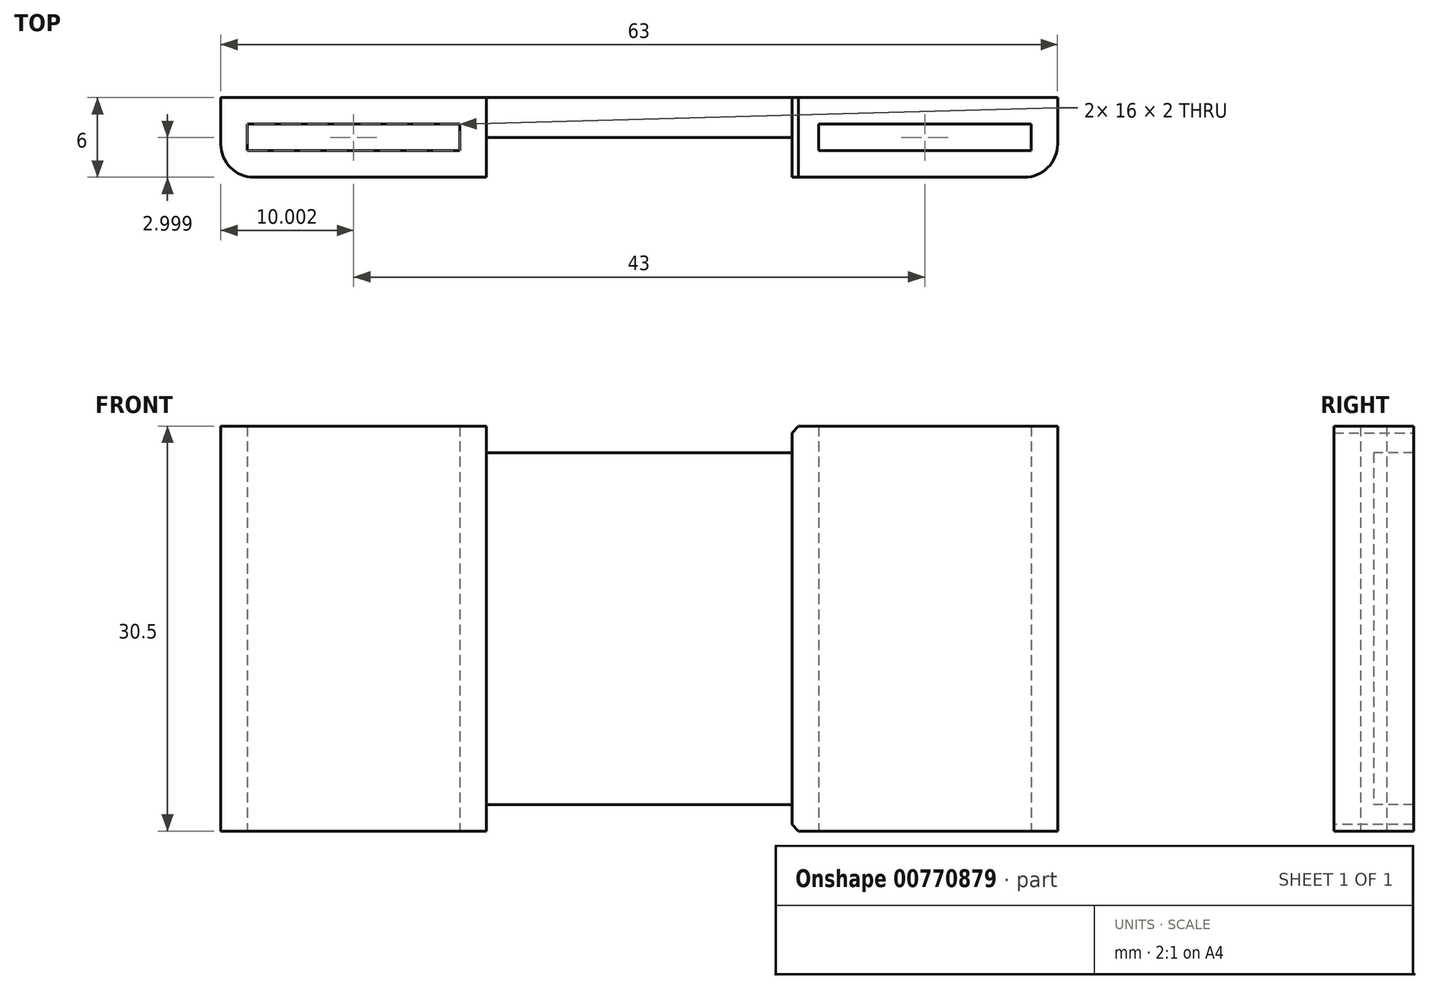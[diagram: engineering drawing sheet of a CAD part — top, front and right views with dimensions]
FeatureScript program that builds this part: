
annotation { "Feature Type Name" : "Feature", "Feature Type Description" : "" }
export const myFeature = defineFeature(function(context is Context, id is Id, definition is map)
    precondition{}
    {
        {
            var Q0;
            Q0=qCreatedBy(makeId("Top.planeOp"),FACE);
            var sketch = newSketch(context, id + "F0", { "sketchPlane" : qUnion([Q0])});
            skLineSegment(sketch, "E0.bottom", {"start": v(-8.67, 15.89) * mm, "end": v(54.33, 15.89) * mm});
            skLineSegment(sketch, "E0.top", {"start": v(11.33, 12.89) * mm, "end": v(34.33, 12.89) * mm});
            skLineSegment(sketch, "E1.top", {"start": v(-8.67, 9.89) * mm, "end": v(11.33, 9.89) * mm});
            skLineSegment(sketch, "E1.right", {"start": v(11.33, 12.89) * mm, "end": v(11.33, 9.89) * mm});
            skLineSegment(sketch, "E2.top", {"start": v(34.33, 9.89) * mm, "end": v(54.33, 9.89) * mm});
            skLineSegment(sketch, "E2.left", {"start": v(34.33, 12.89) * mm, "end": v(34.33, 9.89) * mm});
            skLineSegment(sketch, "E3", {"start": v(-8.67, 15.89) * mm, "end": v(-8.67, 9.89) * mm});
            skLineSegment(sketch, "E4", {"start": v(54.33, 15.89) * mm, "end": v(54.33, 9.89) * mm});
            skLineSegment(sketch, "E5.bottom", {"start": v(-6.67, 13.89) * mm, "end": v(9.33, 13.89) * mm});
            skLineSegment(sketch, "E5.top", {"start": v(-6.67, 11.89) * mm, "end": v(9.33, 11.89) * mm});
            skLineSegment(sketch, "E5.left", {"start": v(-6.67, 13.89) * mm, "end": v(-6.67, 11.89) * mm});
            skLineSegment(sketch, "E5.right", {"start": v(9.33, 13.89) * mm, "end": v(9.33, 11.89) * mm});
            skLineSegment(sketch, "E6.1.0.0", {"start": v(52.33, 13.89) * mm, "end": v(52.33, 11.89) * mm});
            skLineSegment(sketch, "E6.1.0.1", {"start": v(36.33, 13.89) * mm, "end": v(52.33, 13.89) * mm});
            skLineSegment(sketch, "E6.1.0.2", {"start": v(36.33, 11.89) * mm, "end": v(52.33, 11.89) * mm});
            skLineSegment(sketch, "E6.1.0.3", {"start": v(36.33, 13.89) * mm, "end": v(36.33, 11.89) * mm});
            skLineSegment(sketch, "E6.2.0.0", {"start": v(95.33, 13.89) * mm, "end": v(95.33, 11.89) * mm});
            skLineSegment(sketch, "E6.2.0.1", {"start": v(79.33, 13.89) * mm, "end": v(95.33, 13.89) * mm});
            skLineSegment(sketch, "E6.2.0.2", {"start": v(79.33, 11.89) * mm, "end": v(95.33, 11.89) * mm});
            skLineSegment(sketch, "E6.2.0.3", {"start": v(79.33, 13.89) * mm, "end": v(79.33, 11.89) * mm});
            skLineSegment(sketch, "E6.direction1", {"start": v(-6.67, 11.89) * mm, "end": v(36.33, 11.89) * mm, "construction": true});
            skSolve(sketch);
        }
        {
            var Q0;
            Q0=makeQuery(id+"F0.imprint","IMPRINT",FACE,{"disambiguationData":[TD([[makeQuery(id+"F0.imprint","IMPRINT",EDGE,{"derivedFrom":sQuery(id+"F0.wireOp",EDGE,"E0.bottom")}),-1.0]])]});
            extrude(context, id + "F1", {"entities" : qUnion([Q0]), "depth" : 30.5 * mm, "offsetDistance" : 25 * mm});
        }
        {
            var Q0;
            Q0=makeQuery(id+"F1.opExtrude","SWEPT_EDGE",EDGE,{"disambiguationData":[OSD([sQuery(id+"F0.wireOp",EDGE,"E1.top"),sQuery(id+"F0.wireOp",EDGE,"E3")])]});
            var Q1;
            Q1=makeQuery(id+"F1.opExtrude","SWEPT_EDGE",EDGE,{"disambiguationData":[OSD([sQuery(id+"F0.wireOp",EDGE,"E2.top"),sQuery(id+"F0.wireOp",EDGE,"E4")])]});
            fillet(context, id + "F2", {"entities" : qUnion([Q0, Q1]), "radius" : 2.5 * mm, "tangentPropagation" : true, "allowEdgeOverflow" : false});
        }
        {
            var Q0;
            Q0=makeQuery(id+"F1.opExtrude","SWEPT_FACE",FACE,{"disambiguationData":[OSD([sQuery(id+"F0.wireOp",EDGE,"E0.top")])]});
            var sketch = newSketch(context, id + "F3", { "sketchPlane" : qUnion([Q0])});
            skLineSegment(sketch, "E7.bottom", {"start": v(11.33, 30.5) * mm, "end": v(34.33, 30.5) * mm});
            skLineSegment(sketch, "E7.top", {"start": v(11.33, 28.5) * mm, "end": v(34.33, 28.5) * mm});
            skLineSegment(sketch, "E7.left", {"start": v(11.33, 30.5) * mm, "end": v(11.33, 28.5) * mm});
            skLineSegment(sketch, "E7.right", {"start": v(34.33, 30.5) * mm, "end": v(34.33, 28.5) * mm});
            skLineSegment(sketch, "E8.1.0.0", {"start": v(11.33, 2) * mm, "end": v(11.33, 0) * mm});
            skLineSegment(sketch, "E8.1.0.1", {"start": v(11.33, 2) * mm, "end": v(34.33, 2) * mm});
            skLineSegment(sketch, "E8.1.0.2", {"start": v(11.33, 0) * mm, "end": v(34.33, 0) * mm});
            skLineSegment(sketch, "E8.1.0.3", {"start": v(34.33, 2) * mm, "end": v(34.33, 0) * mm});
            skLineSegment(sketch, "E8.2.0.0", {"start": v(11.33, -26.5) * mm, "end": v(11.33, -28.5) * mm});
            skLineSegment(sketch, "E8.2.0.1", {"start": v(11.33, -26.5) * mm, "end": v(34.33, -26.5) * mm});
            skLineSegment(sketch, "E8.2.0.2", {"start": v(11.33, -28.5) * mm, "end": v(34.33, -28.5) * mm});
            skLineSegment(sketch, "E8.2.0.3", {"start": v(34.33, -26.5) * mm, "end": v(34.33, -28.5) * mm});
            skLineSegment(sketch, "E8.direction1", {"start": v(11.33, 28.5) * mm, "end": v(11.33, 0) * mm, "construction": true});
            skSolve(sketch);
        }
        {
            var Q0;
            {var subQ0=sQuery(id+"F3.wireOp",EDGE,"E8.1.0.3");Q0=makeQuery(id+"F3.imprint","IMPRINT",FACE,{"disambiguationData":[TD([[makeQuery(id+"F3.imprint","IMPRINT",EDGE,{"derivedFrom":subQ0}),-1.0]])]});}
            var Q1;
            Q1=makeQuery(id+"F3.imprint","IMPRINT",FACE,{"disambiguationData":[TD([[makeQuery(id+"F3.imprint","IMPRINT",EDGE,{"derivedFrom":sQuery(id+"F3.wireOp",EDGE,"E7.bottom")}),-1.0]])]});
            extrude(context, id + "F4", {"entities" : qUnion([Q0, Q1]), "operationType" : NewBodyOperationType.REMOVE, "oppositeDirection" : true, "depth" : 25 * mm, "offsetDistance" : 25 * mm});
        }
        {
            var Q0;
            Q0=makeQuery(id+"F4.boolean.opBoolean","MERGE",EDGE,{"derivedFrom":[makeQuery(id+"F1.opExtrude","CAP_EDGE",EDGE,{"disambiguationData":[OSD([sQuery(id+"F0.wireOp",EDGE,"E1.right")])],"isStart":false}),makeQuery(id+"F4.opExtrude","SWEPT_EDGE",EDGE,{"disambiguationData":[OSD([sQuery(id+"F3.wireOp",EDGE,"E7.bottom"),sQuery(id+"F3.wireOp",EDGE,"E7.left")])]})]});
            var Q1;
            Q1=makeQuery(id+"F4.boolean.opBoolean","MERGE",EDGE,{"derivedFrom":[makeQuery(id+"F1.opExtrude","CAP_EDGE",EDGE,{"disambiguationData":[OSD([sQuery(id+"F0.wireOp",EDGE,"E2.left")])],"isStart":false}),makeQuery(id+"F4.opExtrude","SWEPT_EDGE",EDGE,{"disambiguationData":[OSD([sQuery(id+"F3.wireOp",EDGE,"E7.bottom"),sQuery(id+"F3.wireOp",EDGE,"E7.right")])]})]});
            var Q2;
            Q2=makeQuery(id+"F4.boolean.opBoolean","COPY",EDGE,{"derivedFrom":makeQuery(id+"F4.opExtrude","SWEPT_EDGE",EDGE,{"disambiguationData":[OSD([sQuery(id+"F0.wireOp",EDGE,"E0.top"),sQuery(id+"F3.wireOp",EDGE,"E8.1.0.2"),sQuery(id+"F3.wireOp",EDGE,"E8.1.0.3")])]})});
            var Q3;
            {var subQ0=sQuery(id+"F0.wireOp",EDGE,"E1.right");Q3=makeQuery(id+"F4.boolean.opBoolean","MERGE",EDGE,{"derivedFrom":[makeQuery(id+"F1.opExtrude","CAP_EDGE",EDGE,{"disambiguationData":[OSD([subQ0])],"isStart":true}),makeQuery(id+"F4.opExtrude","SWEPT_EDGE",EDGE,{"disambiguationData":[OSD([sQuery(id+"F0.wireOp",EDGE,"E0.top"),subQ0,sQuery(id+"F3.wireOp",EDGE,"E8.1.0.2")])]})]});}
            var Q4;
            Q4=makeQuery(id+"F4.boolean.opBoolean","MERGE",EDGE,{"derivedFrom":[makeQuery(id+"F1.opExtrude","CAP_EDGE",EDGE,{"disambiguationData":[OSD([sQuery(id+"F0.wireOp",EDGE,"E2.left")])],"isStart":true}),makeQuery(id+"F4.opExtrude","SWEPT_EDGE",EDGE,{"disambiguationData":[OSD([sQuery(id+"F3.wireOp",EDGE,"E8.1.0.2"),sQuery(id+"F3.wireOp",EDGE,"E8.1.0.3")])]})]});
            var Q5;
            Q5=makeQuery(id+"F4.boolean.opBoolean","COPY",EDGE,{"derivedFrom":makeQuery(id+"F4.opExtrude","CAP_EDGE",EDGE,{"disambiguationData":[OSD([sQuery(id+"F3.wireOp",EDGE,"E8.1.0.1")])],"isStart":true})});
            var Q6;
            Q6=makeQuery(id+"F4.boolean.opBoolean","COPY",EDGE,{"derivedFrom":makeQuery(id+"F4.opExtrude","CAP_EDGE",EDGE,{"disambiguationData":[OSD([sQuery(id+"F3.wireOp",EDGE,"E7.top")])],"isStart":true})});
            chamfer(context, id + "F5", {"entities" : qUnion([Q0, Q1, Q2, Q3, Q4, Q5, Q6]), "width" : .5 * mm, "tangentPropagation" : true});
        }
    });
